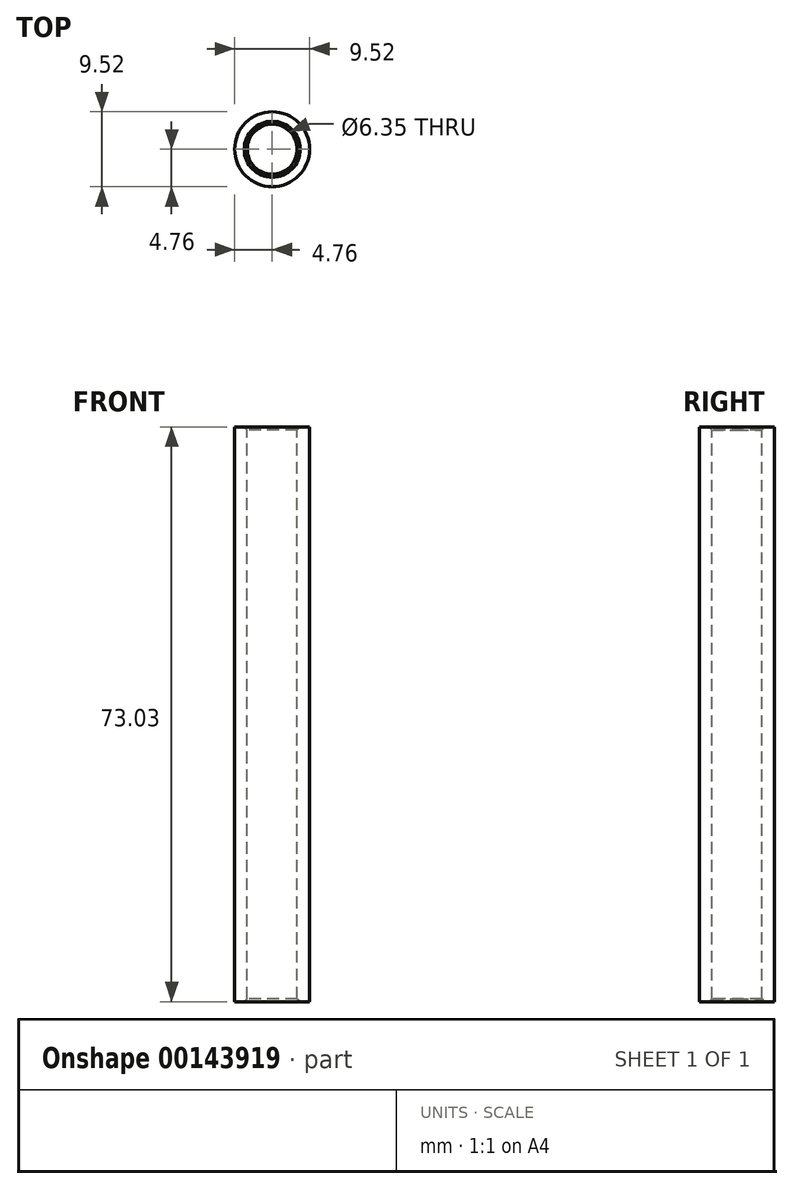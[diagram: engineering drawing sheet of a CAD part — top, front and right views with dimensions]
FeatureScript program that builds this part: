
annotation { "Feature Type Name" : "Feature", "Feature Type Description" : "" }
export const myFeature = defineFeature(function(context is Context, id is Id, definition is map)
    precondition{}
    {
        {
            var Q0;
            Q0=qCreatedBy(makeId("Right.planeOp"),FACE);
            var sketch = newSketch(context, id + "F0", { "sketchPlane" : qUnion([Q0])});
            skLineSegment(sketch, "E0", {"start": v(0, 0) * mm, "end": v(0, -17.02) * mm});
            skLineSegment(sketch, "E1", {"start": v(3.18, 0) * mm, "end": v(4.76, 0) * mm});
            skLineSegment(sketch, "E2", {"start": v(3.18, 0) * mm, "end": v(3.18, 73.03) * mm});
            skLineSegment(sketch, "E3", {"start": v(3.17, 73.03) * mm, "end": v(4.76, 73.03) * mm});
            skLineSegment(sketch, "E4", {"start": v(4.76, 73.03) * mm, "end": v(4.76, 0) * mm});
            skSolve(sketch);
        }
        {
            var Q0;
            Q0=makeQuery(id+"F0.imprint","IMPRINT",FACE,{"disambiguationData":[TD([[makeQuery(id+"F0.imprint","IMPRINT",EDGE,{"derivedFrom":sQuery(id+"F0.wireOp",EDGE,"E1")}),1.0]])]});
            var Q1;
            Q1=sQuery(id+"F0.wireOp",EDGE,"E0");
            revolve(context, id + "F1", {"entities" : qUnion([Q0]), "axis" : qUnion([Q1]), "revolveType" : RevolveType.FULL});
        }
        {
            var Q0;
            Q0=makeQuery(id+"F1.opRevolve","SWEPT_EDGE",EDGE,{"disambiguationData":[OSD([sQuery(id+"F0.wireOp",EDGE,"E2"),sQuery(id+"F0.wireOp",EDGE,"E3")])]});
            var Q1;
            Q1=makeQuery(id+"F1.opRevolve","SWEPT_EDGE",EDGE,{"disambiguationData":[OSD([sQuery(id+"F0.wireOp",EDGE,"E1"),sQuery(id+"F0.wireOp",EDGE,"E2")])]});
            chamfer(context, id + "F2", {"entities" : qUnion([Q0, Q1]), "width" : 0.38 * mm, "tangentPropagation" : true});
        }
    });
